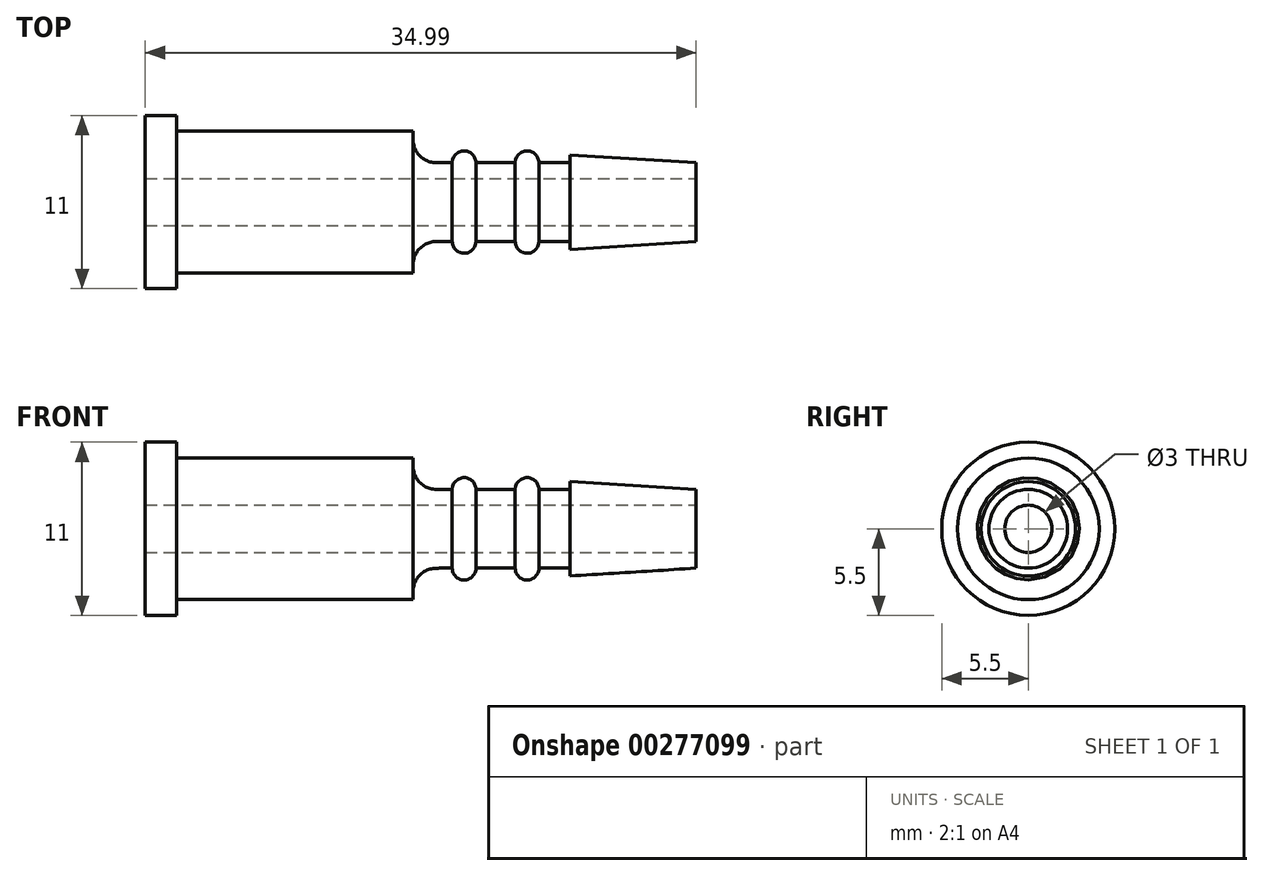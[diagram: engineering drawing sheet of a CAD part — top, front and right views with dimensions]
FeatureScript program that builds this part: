
annotation { "Feature Type Name" : "Feature", "Feature Type Description" : "" }
export const myFeature = defineFeature(function(context is Context, id is Id, definition is map)
    precondition{}
    {
        {
            var Q0;
            Q0=qCreatedBy(makeId("Front.planeOp"),FACE);
            var sketch = newSketch(context, id + "F0", { "sketchPlane" : qUnion([Q0])});
            skLineSegment(sketch, "E0", {"start": v(0, 0) * mm, "end": v(0, 2.5) * mm});
            skLineSegment(sketch, "E1", {"start": v(-8, 3) * mm, "end": v(-8, 2.5) * mm});
            skPoint(sketch, "E2.startSnap0", {"position": v(-13.5, 1) * mm});
            skLineSegment(sketch, "E3", {"start": v(-26.1, 2.5) * mm, "end": v(-26.1, 2.5) * mm});
            skLineSegment(sketch, "E4", {"start": v(-17.99, 4.5) * mm, "end": v(-32.99, 4.5) * mm});
            skPoint(sketch, "E5.visualSharp", {"position": v(-17.99, 2.5) * mm});
            skPoint(sketch, "E6.end.orphan", {"position": v(-33, 0) * mm});
            skLineSegment(sketch, "E7", {"start": v(-32.99, 4.5) * mm, "end": v(-32.99, 5.5) * mm});
            skLineSegment(sketch, "E8", {"start": v(-32.99, 5.5) * mm, "end": v(-34.99, 5.5) * mm});
            skLineSegment(sketch, "E9", {"start": v(-34.99, 0) * mm, "end": v(-34.99, 5.5) * mm});
            skLineSegment(sketch, "E10", {"start": v(0, 0) * mm, "end": v(-34.99, 0) * mm});
            skPoint(sketch, "E11.start.orphan", {"position": v(0, 1) * mm});
            skPoint(sketch, "E12.endSnap0", {"position": v(-9.25, 1.75) * mm});
            skLineSegment(sketch, "E13", {"start": v(0, 2.5) * mm, "end": v(-8, 3) * mm});
            skPoint(sketch, "E14.end.orphan", {"position": v(-8, 3.5) * mm});
            skPoint(sketch, "E12.end.orphan", {"position": v(-9.25, 3.75) * mm});
            skPoint(sketch, "E15.start.orphan", {"position": v(-10.5, 1) * mm});
            skPoint(sketch, "E16.orphan", {"position": v(-12, 1) * mm});
            skPoint(sketch, "E17.end.orphan", {"position": v(-16.5, 1) * mm});
            skPoint(sketch, "E17.start.orphan", {"position": v(-15, 1) * mm});
            skLineSegment(sketch, "E18", {"start": v(-8, 2.5) * mm, "end": v(-9.99, 2.5) * mm});
            skLineSegment(sketch, "E19", {"start": v(-11.49, 2.5) * mm, "end": v(-13.99, 2.5) * mm});
            skLineSegment(sketch, "E20", {"start": v(-15.49, 2.5) * mm, "end": v(-16.49, 2.5) * mm});
            skArc(sketch, "E21", {"start": v(-9.99, 2.5) * mm, "mid": v(-10.74, 3.25) * mm, "end": v(-11.49, 2.5) * mm});
            skArc(sketch, "E22", {"start": v(-13.99, 2.5) * mm, "mid": v(-14.74, 3.25) * mm, "end": v(-15.49, 2.5) * mm});
            skLineSegment(sketch, "E23", {"start": v(-17.99, 4.5) * mm, "end": v(-17.99, 4) * mm});
            skArc(sketch, "E24.filletArc", {"start": v(-17.99, 4) * mm, "mid": v(-17.55, 2.94) * mm, "end": v(-16.49, 2.5) * mm});
            skSolve(sketch);
        }
        {
            var Q0;
            Q0=makeQuery(id+"F0.imprint","IMPRINT",FACE,{"disambiguationData":[TD([[makeQuery(id+"F0.imprint","IMPRINT",EDGE,{"derivedFrom":sQuery(id+"F0.wireOp",EDGE,"E0")}),1.0]])]});
            var Q1;
            Q1=sQuery(id+"F0.wireOp",EDGE,"E10");
            revolve(context, id + "F1", {"entities" : qUnion([Q0]), "axis" : qUnion([Q1]), "revolveType" : RevolveType.FULL});
        }
        {
            var Q0;
            Q0=makeQuery(id+"F1.opRevolve","SWEPT_FACE",FACE,{"disambiguationData":[OSD([sQuery(id+"F0.wireOp",EDGE,"E0")])]});
            var sketch = newSketch(context, id + "F2", { "sketchPlane" : qUnion([Q0])});
            skCircle(sketch, "E25", {"center": v(0, 0) * mm, "radius": 1.5 * mm});
            skSolve(sketch);
        }
        {
            var Q0;
            Q0=makeQuery(id+"F2.imprint","IMPRINT",FACE,{"disambiguationData":[TD([[makeQuery(id+"F2.imprint","IMPRINT",EDGE,{"derivedFrom":sQuery(id+"F2.wireOp",EDGE,"E25")}),1.0]])]});
            extrude(context, id + "F3", {"entities" : qUnion([Q0]), "operationType" : NewBodyOperationType.REMOVE, "oppositeDirection" : true, "depth" : 37 * mm});
        }
    });
